# Revit family: QF_MARCO_MILKPAL WHITE
name_source: partatom
category: Specialty Equipment
units: mm (PartAtom-declared; Revit-internal decimal feet)

## family parameters
Always vertical = Yes
Cut with Voids When Loaded = No
Enable Cutting in Views = No
Maintain Annotation Orientation = No
Part Type = Normal
Room Calculation Point = No
Round Connector Dimension = Use Diameter
Shared = No
Work Plane-Based = No

## types (1)
- MILKPAL WHITE
    Apparent Power = 0 VA
    BTUH = 0.0 Btu/h
    Chilled Water Flow = 0 GPM
    Chilled Water Maximum Pressure = 0.00 psi
    Chilled Water Minimum Pressure = 0.00 psi
    Chilled Water Return Connection Height = 0 "
    Chilled Water Return RI Height = 0 "
    Chilled Water Return Size = 1"
    Chilled Water Supply Connection Height = 0 "
    Chilled Water Supply RI Height = 0 "
    Chilled Water Supply Size = 1"
    Chilled Water Temperature = 0 °F
    Cold Water Connection Height = 0 "
    Cold Water Flow = 0 GPM
    Cold Water Maximum Pressure = 0.00 psi
    Cold Water Minimum Pressure = 0.00 psi
    Cold Water RI Height = 0 "
    Cold Water Size = 1"
    Cold Water Temperature Recommended = 0 °F
    Conn Conduit = Yes
    Conn Plug = NEMA L6-20P
    Cycle = 60 Hz
    Default Elevation = 0 "
    Depth = 21 "
    Description = MILKPAL WHITE
    Elec Conn Connection Height = 0 "
    Elec Conn RI Height = 0 "
    Exhaust RI Height = 0 "
    Exhaust Static Press = 0.00 in-wg
    Exhaust Vent Depth = 0 "
    Exhaust Vent Diameter = 0.75 "
    Exhaust Vent Width = 0 "
    Exhaust Volume = 0 CFM
    FL Amps = 0 A
    Foodservice Equipment Identifier = Yes
    HP = 1/8
    Height = 15.5 "
    Hot Water Connection Height = 0 "
    Hot Water Consumption = 0 GPM
    Hot Water Flow = 0 GPM
    Hot Water Maximum Pressure = 0.00 psi
    Hot Water Minimum Pressure = 0.00 psi
    Hot Water RI Height = 0 "
    Hot Water Size = 1"
    Hot Water Temperature = 0 °F
    Identify Quantity as Lot = Yes
    Length = 7.8 "
    MU Air RI Height = 0 "
    MU Air Static Press = 0.00 in-wg
    MU Air Vent Depth = 0 "
    MU Air Vent Diameter = 0.75 "
    MU Air Vent Width = 0 "
    MU Air Volume = 0 CFM
    Manufacturer = MARCO
    Max Overcurrent Protection = 0 A
    Min Ckt Ampacity = 0 A
    Model = MILKPAL WHITE
    Number of Poles = 1
    Phase = 1
    Refrigerant Type = R290
    Refrigerant Volume = 0.00 kip
    Volts = 120 V
    Watts = 2800 W
    Weight in Pounds = 47.5

## geometry (parser evidence)
native form markers: Sweep x2
no freeform markers — native parametric forms only
